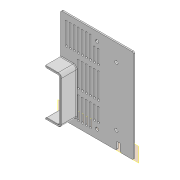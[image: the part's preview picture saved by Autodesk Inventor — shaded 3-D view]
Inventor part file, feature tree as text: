
AUTODESK INVENTOR PART (.ipt)
format: ipt  version: 2020 (Build 240168000, 168)  size: 846,848 bytes
history: native  units: mm
features: extrude x10, sketch x10, other x9, fillet x6, mirror x1
ambient origin geometry x8: Origin, YZ Plane, XZ Plane, XY Plane, X Axis, Y Axis, Z Axis, Center Point
bodies: Body1 (feature_tree)
feature tree (36):
  other  "Sólido1"
  other  "Plano de trabalho1"
  extrude  "Extrusão1"  Depth=0.5mm
  fillet  "Arredondamento2"  Radius=1.0mm
  extrude  "Extrusão5"  Depth=0.5mm
  mirror  "Espelhamento1"
  extrude  "Extrusão6"  Depth=4.5mm
  sketch  "Esboço7"  dims[d7=0.5mm d8=4.5mm]
  extrude  "Extrusão7"  Depth=4.5mm
  extrude  "Extrusão8"  Depth=10.0mm
  sketch  "Esboço9"  dims[d11=18.0mm d12=23.0mm]
  extrude  "Extrusão9"  Depth=23.0mm
  extrude  "Extrusão10"  Depth=23.0mm
  fillet  "Arredondamento3"  Radius=32.0mm
  fillet  "Arredondamento4"  Radius=32.0mm
  extrude  "Extrusão11"  Depth=26.0mm
  extrude  "Extrusão12"  Depth=3.2mm
  fillet  "Arredondamento5"  Radius=2.0mm
  extrude  "Extrusão13"  Depth=3.2mm
  fillet  "Arredondamento6"  Radius=6.0mm
  fillet  "Arredondamento7"  Radius=30.0mm
  sketch  "Esboço1"  dims[d0=0.5mm d1=0.5mm d2=1.0mm]
  other  "Referência1"
  other  "Referência2"
  sketch  "Esboço5"  dims[d3=1.0mm d4=0.5mm]
  sketch  "Esboço6"  dims[d5=0.5mm d6=4.5mm]
  sketch  "Esboço8"  dims[d9=10.0mm d10=10.0mm]
  other  "Contorno projetado3"
  sketch  "Esboço10"  dims[d13=23.0mm d14=31.0mm d15=32.0mm d16=32.0mm]
  other  "Contorno projetado4"
  sketch  "Esboço11"  dims[d17=31.0mm d18=26.0mm]
  sketch  "Esboço12"  dims[d19=3.2mm d20=3.2mm]
  sketch  "Esboço13"  dims[d21=70.0mm d23=6.0mm d24=10.0mm d26=10.0mm d28=2.0mm d29=0.0mm d30=3.2mm d31=6.0mm d32=30.0mm d34=6.0mm d35=10.0mm d37=10.0mm d39=3.2mm d40=6.0mm d41=50.0mm d43=6.0mm d44=10.0mm d46=10.0mm d48=20.0mm d50=6.0mm d51=10.0mm d53=10.0mm d65=2.0mm d66=70.0mm d67=2.2mm d68=0.0mm d69=32.0mm d70=26.0mm d71=19.446305mm d72=32.276848mm d73=3.2mm d74=110.0mm d76=6.0mm d77=10.0mm d79=10.0mm d81=2.2mm d82=0.0mm d83=77.0mm d84=21.0mm d85=2.0mm d86=0.0mm d87=2.0mm d88=0.0mm d90=5.0mm d91=19.8mm d92=12.0mm d93=8.0mm d94=2.0mm d95=0.0mm d96=2.0mm d97=0.0mm d98=2.0mm d99=0.5mm d100=70.0mm d101=140.0mm d102=25.380618mm d103=5.0mm d104=5.0mm d105=44.0mm d106=44.0mm d107=2.0mm d108=0.0mm d109=13.0mm d110=2.0mm d111=0.0mm d112=2.0mm d113=3.0mm d114=23.0mm d115=0.0mm d116=0.5mm d117=1.0mm]
  other  "Calorímetro.iam"
  other  "suporte_fechamento:2"
  other  "suporte_fechamento:3"
